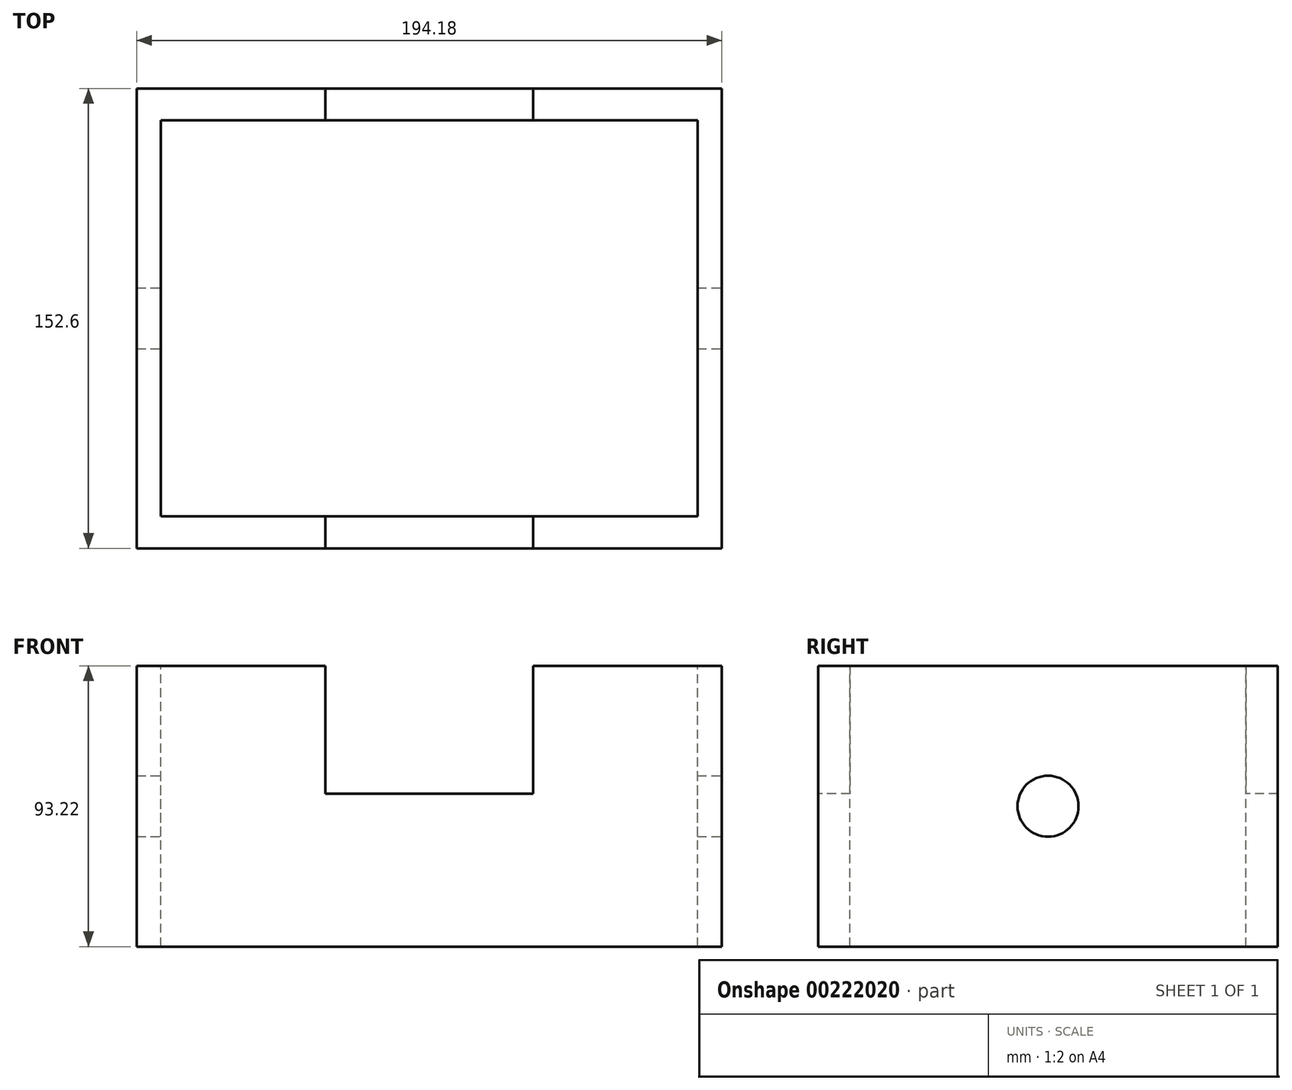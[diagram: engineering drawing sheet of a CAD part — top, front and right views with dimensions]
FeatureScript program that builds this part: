
annotation { "Feature Type Name" : "Feature", "Feature Type Description" : "" }
export const myFeature = defineFeature(function(context is Context, id is Id, definition is map)
    precondition{}
    {
        {
            var Q0;
            Q0=qCreatedBy(makeId("Top.planeOp"),FACE);
            var sketch = newSketch(context, id + "F0", { "sketchPlane" : qUnion([Q0])});
            skLineSegment(sketch, "E0.bottom", {"start": v(97.1, -76.3) * mm, "end": v(-97.1, -76.3) * mm});
            skLineSegment(sketch, "E0.top", {"start": v(97.1, 76.3) * mm, "end": v(-97.1, 76.3) * mm});
            skLineSegment(sketch, "E0.left", {"start": v(97.1, -76.3) * mm, "end": v(97.1, 76.3) * mm});
            skLineSegment(sketch, "E0.right", {"start": v(-97.1, -76.3) * mm, "end": v(-97.1, 76.3) * mm});
            skPoint(sketch, "E0.middle", {"position": v(0, 0) * mm});
            skSolve(sketch);
        }
        {
            var Q0;
            Q0 = qSketchRegion(id + "F0", true);
            extrude(context, id + "F1", {"entities" : qUnion([Q0]), "depth" : 93.22 * mm});
        }
        {
            var Q0;
            Q0=makeQuery(id+"F1.opExtrude","CAP_FACE",FACE,{"disambiguationData":[OSD([sQuery(id+"F0.wireOp",EDGE,"E0.bottom"),sQuery(id+"F0.wireOp",EDGE,"E0.top"),sQuery(id+"F0.wireOp",EDGE,"E0.left"),sQuery(id+"F0.wireOp",EDGE,"E0.right")])],"isStart":false});
            var sketch = newSketch(context, id + "F2", { "sketchPlane" : qUnion([Q0])});
            skLineSegment(sketch, "E1.bottom", {"start": v(89.07, -65.72) * mm, "end": v(-89.07, -65.72) * mm});
            skLineSegment(sketch, "E1.top", {"start": v(89.07, 65.72) * mm, "end": v(-89.07, 65.72) * mm});
            skLineSegment(sketch, "E1.left", {"start": v(89.07, -65.72) * mm, "end": v(89.07, 65.72) * mm});
            skLineSegment(sketch, "E1.right", {"start": v(-89.07, -65.72) * mm, "end": v(-89.07, 65.72) * mm});
            skPoint(sketch, "E1.middle", {"position": v(0, 0) * mm});
            skSolve(sketch);
        }
        {
            var Q0;
            Q0 = qSketchRegion(id + "F2", true);
            extrude(context, id + "F3", {"entities" : qUnion([Q0]), "operationType" : NewBodyOperationType.REMOVE, "oppositeDirection" : true, "depth" : 149.6 * mm});
        }
        {
            var Q0;
            Q0=makeQuery(id+"F1.opExtrude","SWEPT_FACE",FACE,{"disambiguationData":[OSD([sQuery(id+"F0.wireOp",EDGE,"E0.bottom")])]});
            var sketch = newSketch(context, id + "F4", { "sketchPlane" : qUnion([Q0])});
            skLineSegment(sketch, "E2.bottom", {"start": v(34.5, 50.74) * mm, "end": v(-34.5, 50.74) * mm});
            skLineSegment(sketch, "E2.top", {"start": v(34.5, 135.7) * mm, "end": v(-34.5, 135.7) * mm});
            skLineSegment(sketch, "E2.left", {"start": v(34.5, 50.74) * mm, "end": v(34.5, 135.7) * mm});
            skLineSegment(sketch, "E2.right", {"start": v(-34.5, 50.74) * mm, "end": v(-34.5, 135.7) * mm});
            skPoint(sketch, "E2.middle", {"position": v(0, 93.22) * mm});
            skSolve(sketch);
        }
        {
            var Q0;
            Q0 = qSketchRegion(id + "F4", true);
            extrude(context, id + "F5", {"entities" : qUnion([Q0]), "operationType" : NewBodyOperationType.REMOVE, "oppositeDirection" : true, "depth" : 236.73 * mm});
        }
        {
            var Q0;
            Q0=makeQuery(id+"F1.opExtrude","SWEPT_FACE",FACE,{"disambiguationData":[OSD([sQuery(id+"F0.wireOp",EDGE,"E0.left")])]});
            var sketch = newSketch(context, id + "F6", { "sketchPlane" : qUnion([Q0])});
            skCircle(sketch, "E3", {"center": v(0, 46.6) * mm, "radius": 10.11 * mm});
            skPoint(sketch, "E3.centerSnap0", {"position": v(-76.3, 46.6) * mm});
            skSolve(sketch);
        }
        {
            var Q0;
            Q0 = qSketchRegion(id + "F6", true);
            extrude(context, id + "F7", {"entities" : qUnion([Q0]), "operationType" : NewBodyOperationType.REMOVE, "oppositeDirection" : true, "depth" : 293.62 * mm});
        }
    });
